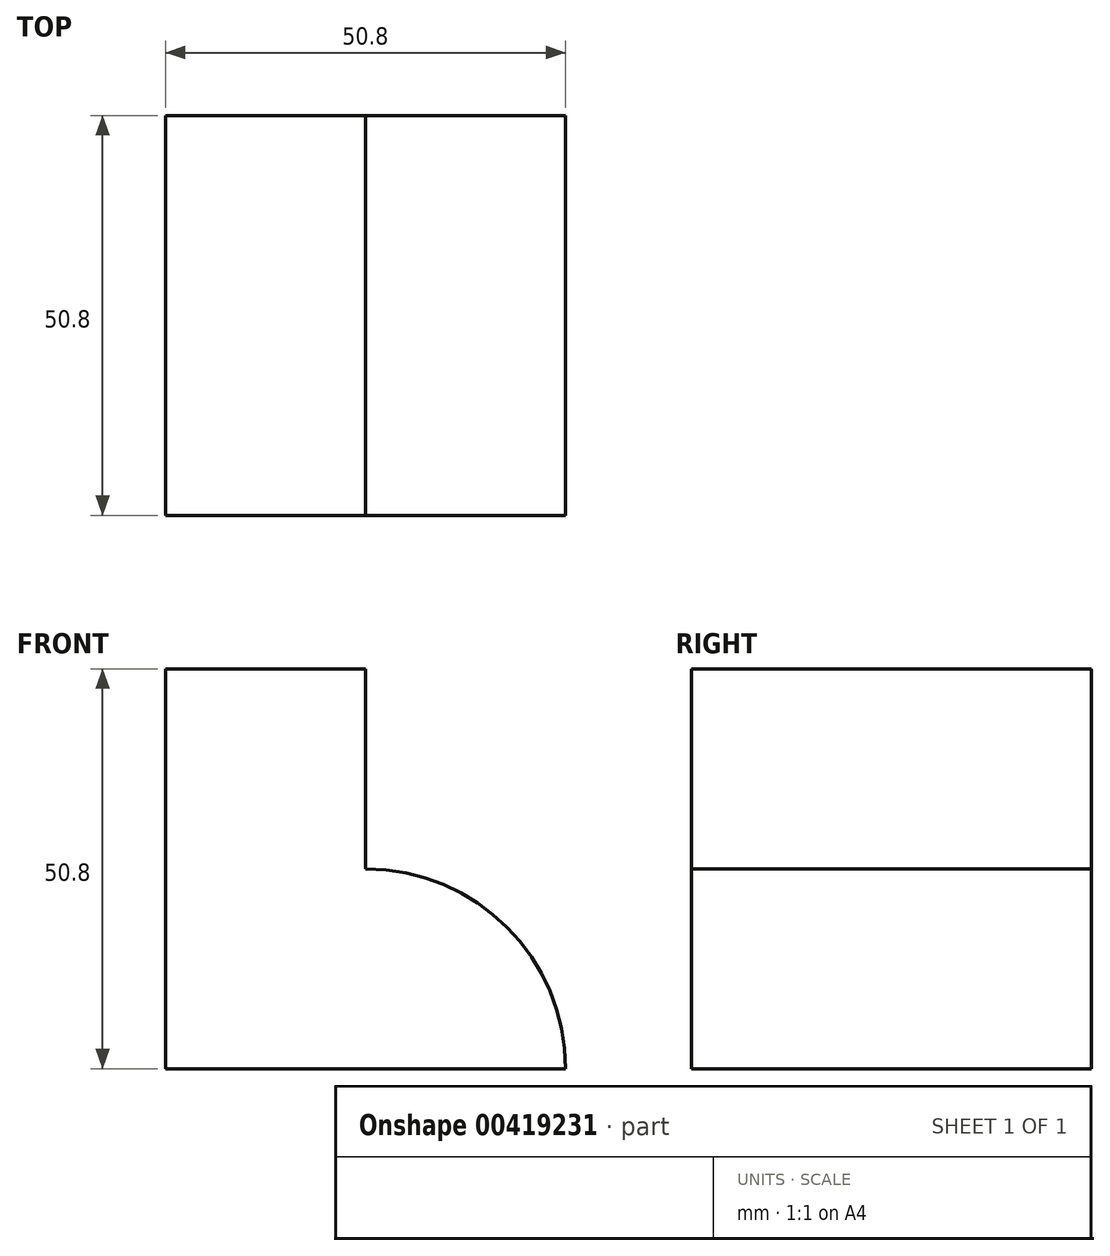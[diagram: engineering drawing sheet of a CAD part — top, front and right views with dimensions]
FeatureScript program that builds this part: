
annotation { "Feature Type Name" : "Feature", "Feature Type Description" : "" }
export const myFeature = defineFeature(function(context is Context, id is Id, definition is map)
    precondition{}
    {
        {
            var Q0;
            Q0=qCreatedBy(makeId("Front.planeOp"),FACE);
            var sketch = newSketch(context, id + "F0", { "sketchPlane" : qUnion([Q0])});
            skLineSegment(sketch, "E0", {"start": v(0, 0) * mm, "end": v(-50.8, 0) * mm});
            skLineSegment(sketch, "E1", {"start": v(-50.8, 0) * mm, "end": v(-50.8, 50.8) * mm});
            skLineSegment(sketch, "E2", {"start": v(-50.8, 50.8) * mm, "end": v(-25.4, 50.8) * mm});
            skLineSegment(sketch, "E3", {"start": v(-25.4, 50.8) * mm, "end": v(-25.4, 25.4) * mm});
            skArc(sketch, "E4", {"start": v(0, 0) * mm, "mid": v(-7.44, 17.96) * mm, "end": v(-25.4, 25.4) * mm});
            skPoint(sketch, "E5.start.orphan", {"position": v(0, 25.4) * mm});
            skSolve(sketch);
        }
        {
            var Q0;
            Q0=makeQuery(id+"F0.imprint","IMPRINT",FACE,{"disambiguationData":[TD([[makeQuery(id+"F0.imprint","IMPRINT",EDGE,{"derivedFrom":sQuery(id+"F0.wireOp",EDGE,"E0")}),-1.0]])]});
            extrude(context, id + "F1", {"entities" : qUnion([Q0]), "depth" : 50.8 * mm});
        }
    });
